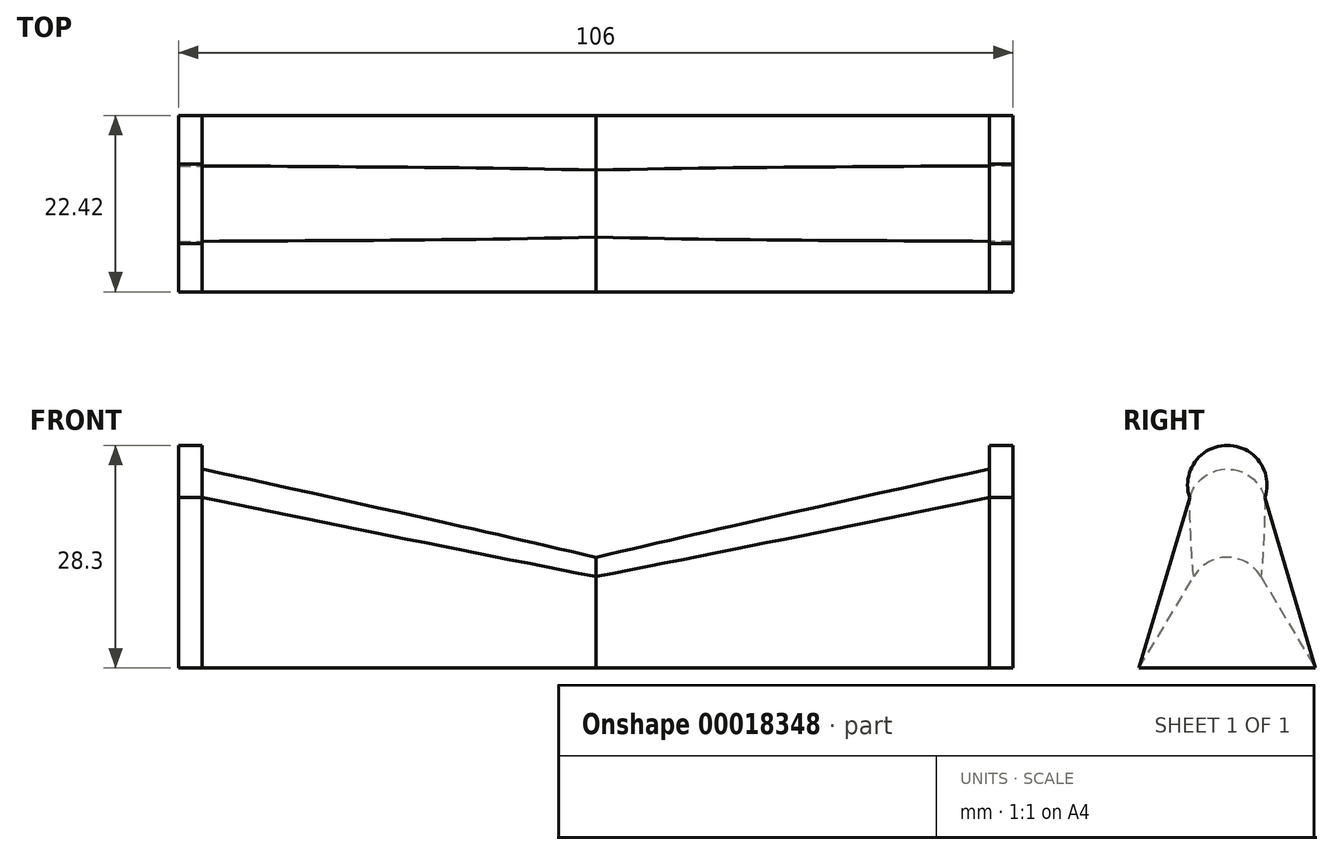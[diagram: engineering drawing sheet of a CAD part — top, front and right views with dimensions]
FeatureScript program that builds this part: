
annotation { "Feature Type Name" : "Feature", "Feature Type Description" : "" }
export const myFeature = defineFeature(function(context is Context, id is Id, definition is map)
    precondition{}
    {
        {
            var Q0;
            Q0=qCreatedBy(makeId("Right.planeOp"),FACE);
            var sketch = newSketch(context, id + "F0", { "sketchPlane" : qUnion([Q0])});
            skLineSegment(sketch, "E0", {"start": v(0, 0) * mm, "end": v(-11.2, -37.79) * mm});
            skLineSegment(sketch, "E1", {"start": v(-11.2, -37.79) * mm, "end": v(11.2, -37.79) * mm});
            skLineSegment(sketch, "E2", {"start": v(11.2, -37.79) * mm, "end": v(0, 0) * mm});
            skSolve(sketch);
        }
        {
            var Q0;
            Q0=qCreatedBy(makeId("Right.planeOp"),FACE);
            cPlane(context, id + "F1", {"entities" : qUnion([Q0]), "cplaneType" : CPlaneType.OFFSET, "offset" : 50 * mm, "width" : 150 * mm, "height" : 150 * mm});
        }
        {
            var Q0;
            Q0=qCreatedBy(id+"F1.planeOp",FACE);
            var sketch = newSketch(context, id + "F2", { "sketchPlane" : qUnion([Q0])});
            skLineSegment(sketch, "E3.0", {"start": v(-11.2, -37.79) * mm, "end": v(11.2, -37.79) * mm});
            skLineSegment(sketch, "E4", {"start": v(-11.2, -37.79) * mm, "end": v(0, -19.02) * mm});
            skLineSegment(sketch, "E5", {"start": v(0, -19.02) * mm, "end": v(11.2, -37.79) * mm});
            skSolve(sketch);
        }
        {
            var Q0;
            Q0=makeQuery(id+"F0.imprint","IMPRINT",FACE,{"disambiguationData":[TD([[makeQuery(id+"F0.imprint","IMPRINT",EDGE,{"derivedFrom":sQuery(id+"F0.wireOp",EDGE,"E0")}),1.0]])]});
            var Q1;
            Q1=makeQuery(id+"F2.imprint","IMPRINT",FACE,{"disambiguationData":[TD([[makeQuery(id+"F2.imprint","IMPRINT",EDGE,{"derivedFrom":sQuery(id+"F2.wireOp",EDGE,"E3.0")}),1.0]])]});
            loft(context, id + "F3", {"sheetProfilesArray" : [{ "sheetProfileEntities" : qUnion([Q0]) }, { "sheetProfileEntities" : qUnion([Q1]) }]});
        }
        {
            var Q0;
            Q0=makeQuery(id+"F3.opLoft","SWEPT_EDGE",EDGE,{"disambiguationData":[OSD([sQuery(id+"F0.wireOp",EDGE,"E0"),sQuery(id+"F0.wireOp",EDGE,"E2"),sQuery(id+"F2.wireOp",EDGE,"E4"),sQuery(id+"F2.wireOp",EDGE,"E5")])]});
            fillet(context, id + "F4", {"entities" : qUnion([Q0]), "radius" : 5 * mm, "tangentPropagation" : true, "allowEdgeOverflow" : false});
        }
        {
            var Q0;
            Q0=makeQuery(id+"F3.opLoft","CAP_FACE",FACE,{"disambiguationData":[OSD([makeQuery(id+"F0.imprint","IMPRINT",FACE,{"disambiguationData":[TD([[makeQuery(id+"F0.imprint","IMPRINT",EDGE,{"derivedFrom":sQuery(id+"F0.wireOp",EDGE,"E0")}),1.0]])]})])],"isStart":true});
            var sketch = newSketch(context, id + "F5", { "sketchPlane" : qUnion([Q0])});
            skArc(sketch, "E6", {"start": v(4.78, -16.13) * mm, "mid": v(0, -9.5) * mm, "end": v(-4.78, -16.13) * mm});
            skSolve(sketch);
        }
        {
            var Q0;
            Q0=makeQuery(id+"F5.imprint","IMPRINT",FACE,{"disambiguationData":[TD([[makeQuery(id+"F5.imprint","IMPRINT",EDGE,{"derivedFrom":sQuery(id+"F5.wireOp",EDGE,"E6")}),1.0]])]});
            var Q1;
            {var subQ0=sQuery(id+"F0.wireOp",EDGE,"E0");var subQ1=sQuery(id+"F0.wireOp",EDGE,"E1");var subQ2=sQuery(id+"F0.wireOp",EDGE,"E2");var subQ4=makeQuery(id+"F0.imprint","INTERSECT",VERTEX,{"derivedFrom":[subQ1,subQ2]});var subQ6=makeQuery(id+"F0.imprint","IMPRINT",EDGE,{"derivedFrom":subQ1});var subQ8=makeQuery(id+"F0.imprint","INTERSECT",VERTEX,{"derivedFrom":[subQ0,subQ1]});Q1=makeQuery(id+"F5.imprint","IMPRINT",FACE,{"disambiguationData":[TD([[makeQuery(id+"F5.imprint","IMPRINT",EDGE,{"derivedFrom":makeQuery(id+"F3.opLoft","MID_CAP_EDGE",EDGE,{"disambiguationData":[OSD([subQ0,subQ1,subQ2]),TDD([subQ8,subQ4,subQ6])],"capPos":0.0})}),-1.0]])]});}
            extrude(context, id + "F6", {"entities" : qUnion([Q0, Q1]), "operationType" : NewBodyOperationType.ADD, "depth" : 3 * mm});
        }
        {
            var Q0;
            Q0=makeQuery(id+"F3.opLoft","SWEPT_BODY",BODY,{"disambiguationData":[OSD([makeQuery(id+"F0.imprint","IMPRINT",FACE,{"disambiguationData":[TD([[makeQuery(id+"F0.imprint","IMPRINT",EDGE,{"derivedFrom":sQuery(id+"F0.wireOp",EDGE,"E0")}),1.0]])]}),makeQuery(id+"F2.imprint","IMPRINT",FACE,{"disambiguationData":[TD([[makeQuery(id+"F2.imprint","IMPRINT",EDGE,{"derivedFrom":sQuery(id+"F2.wireOp",EDGE,"E3.0")}),1.0]])]})])]});
            var Q1;
            Q1=qCreatedBy(id+"F1.planeOp",FACE);
            mirror(context, id + "F7", {"operationType" : NewBodyOperationType.ADD, "entities" : qUnion([Q0]), "mirrorPlane" : qUnion([Q1])});
        }
    });
